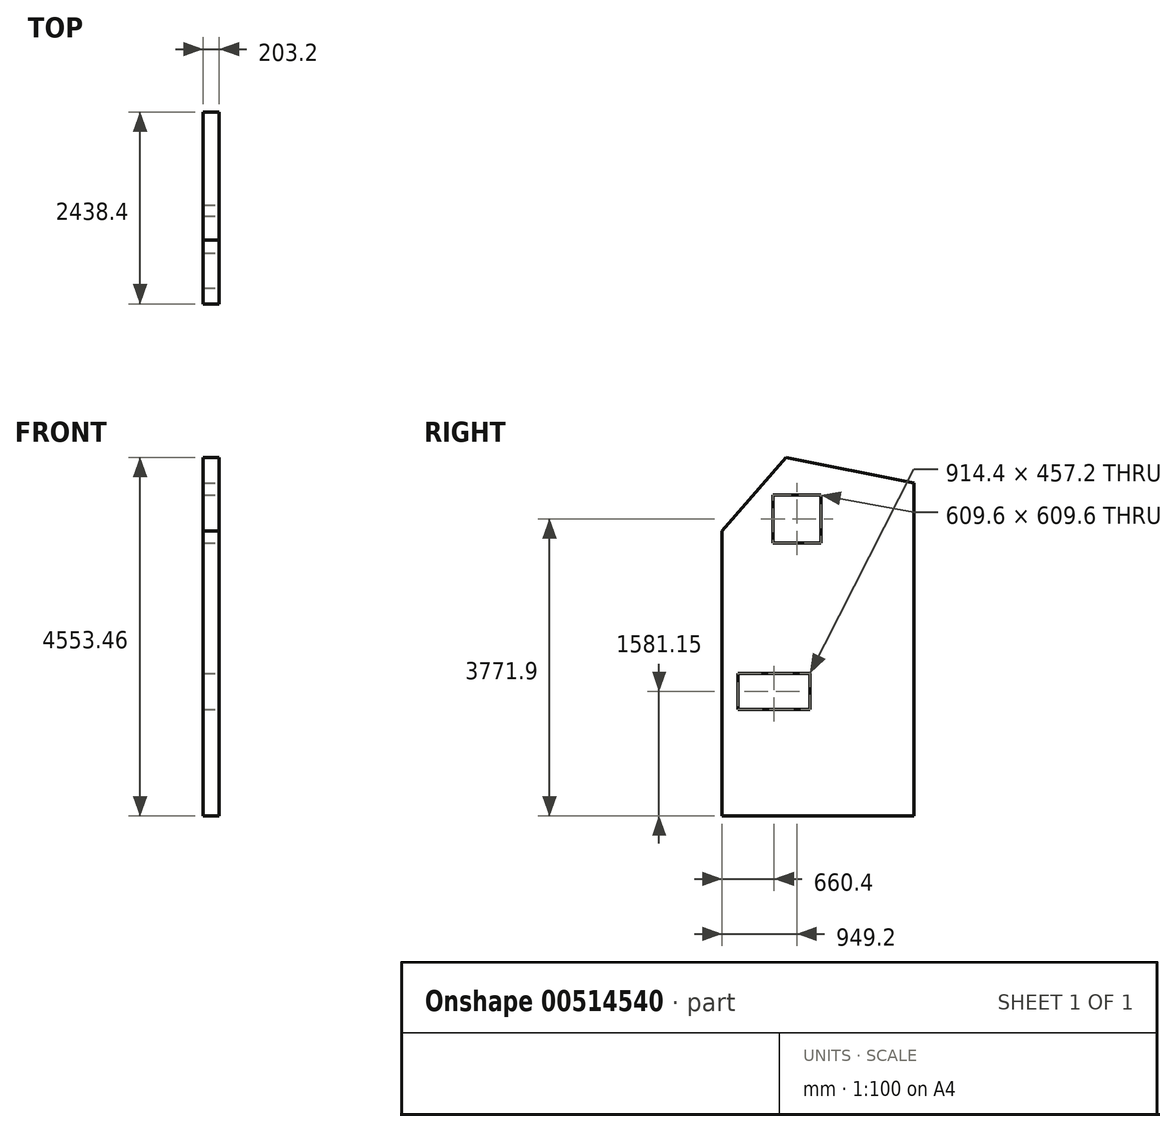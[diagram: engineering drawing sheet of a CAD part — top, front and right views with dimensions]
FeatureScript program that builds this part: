
annotation { "Feature Type Name" : "Feature", "Feature Type Description" : "" }
export const myFeature = defineFeature(function(context is Context, id is Id, definition is map)
    precondition{}
    {
        {
            var Q0;
            Q0=qCreatedBy(makeId("Right.planeOp"),FACE);
            var sketch = newSketch(context, id + "F0", { "sketchPlane" : qUnion([Q0])});
            skLineSegment(sketch, "E0.bottom", {"start": v(1219.2, 2353.82) * mm, "end": v(-1219.2, 2353.82) * mm});
            skLineSegment(sketch, "E0.top", {"start": v(1219.2, -2353.82) * mm, "end": v(-1219.2, -2353.82) * mm});
            skLineSegment(sketch, "E0.left", {"start": v(1219.2, 2353.82) * mm, "end": v(1219.2, -2353.82) * mm});
            skLineSegment(sketch, "E0.right", {"start": v(-1219.2, 2353.82) * mm, "end": v(-1219.2, -2353.82) * mm});
            skPoint(sketch, "E0.middle", {"position": v(0, 0) * mm});
            skSolve(sketch);
        }
        {
            var Q0;
            Q0=makeQuery(id+"F0.imprint","IMPRINT",FACE,{"disambiguationData":[TD([[makeQuery(id+"F0.imprint","IMPRINT",EDGE,{"derivedFrom":sQuery(id+"F0.wireOp",EDGE,"E0.bottom")}),1.0]])]});
            extrude(context, id + "F1", {"entities" : qUnion([Q0]), "depth" : 203.2 * mm, "offsetDistance" : 25.4 * mm});
        }
        {
            var Q0;
            Q0=qCreatedBy(makeId("Front.planeOp"),FACE);
            var sketch = newSketch(context, id + "F2", { "sketchPlane" : qUnion([Q0])});
            skLineSegment(sketch, "E1", {"start": v(0, 0) * mm, "end": v(0, -38) * mm});
            skSolve(sketch);
        }
        {
            var Q0;
            Q0=makeQuery(id+"F1.opExtrude","SWEPT_BODY",BODY,{"disambiguationData":[OSD([sQuery(id+"F0.wireOp",EDGE,"E0.bottom"),sQuery(id+"F0.wireOp",EDGE,"E0.top"),sQuery(id+"F0.wireOp",EDGE,"E0.left"),sQuery(id+"F0.wireOp",EDGE,"E0.right")])]});
            var Q1;
            Q1=sQuery(id+"F2.wireOp",EDGE,"E1");
            transform(context, id + "F3", {"entities" : qUnion([Q0]), "transformType" : TransformType.ROTATION, "transformAxis" : qUnion([Q1]), "angle" : 180 * degree, "makeCopy" : false});
        }
        {
            var Q0;
            Q0=makeQuery(id+"F1.opExtrude","CAP_FACE",FACE,{"disambiguationData":[OSD([sQuery(id+"F0.wireOp",EDGE,"E0.bottom"),sQuery(id+"F0.wireOp",EDGE,"E0.top"),sQuery(id+"F0.wireOp",EDGE,"E0.left"),sQuery(id+"F0.wireOp",EDGE,"E0.right")])],"isStart":true});
            var sketch = newSketch(context, id + "F4", { "sketchPlane" : qUnion([Q0])});
            skLineSegment(sketch, "E2", {"start": v(-407.32, 276.86) * mm, "end": v(-407.32, 46.48) * mm});
            skLineSegment(sketch, "E3", {"start": v(-407.32, 2199.64) * mm, "end": v(-407.32, 46.48) * mm});
            skLineSegment(sketch, "E4", {"start": v(1219.2, 46.48) * mm, "end": v(1219.2, 1875.28) * mm});
            skLineSegment(sketch, "E5", {"start": v(-1219.2, 46.48) * mm, "end": v(-1219.2, 1265.68) * mm});
            skLineSegment(sketch, "E6", {"start": v(-1219.2, 46.48) * mm, "end": v(-407.32, 46.48) * mm});
            skLineSegment(sketch, "E7", {"start": v(-1219.2, 1265.68) * mm, "end": v(-407.32, 2199.64) * mm});
            skLineSegment(sketch, "E8", {"start": v(-1219.2, 1265.68) * mm, "end": v(-407.32, 1265.68) * mm});
            skLineSegment(sketch, "E9", {"start": v(1219.2, 1875.28) * mm, "end": v(-407.32, 2199.64) * mm});
            skSolve(sketch);
        }
        {
            var Q0;
            {var subQ3=sQuery(id+"F4.wireOp",EDGE,"E7");Q0=makeQuery(id+"F4.imprint","IMPRINT",FACE,{"disambiguationData":[TD([[makeQuery(id+"F4.imprint","IMPRINT",EDGE,{"derivedFrom":subQ3}),1.0]])]});}
            extrude(context, id + "F5", {"entities" : qUnion([Q0]), "operationType" : NewBodyOperationType.REMOVE, "oppositeDirection" : true, "depth" : 203.2 * mm, "offsetDistance" : 25.4 * mm});
        }
        {
            var Q0;
            Q0=makeQuery(id+"F1.opExtrude","CAP_FACE",FACE,{"disambiguationData":[OSD([sQuery(id+"F0.wireOp",EDGE,"E0.bottom"),sQuery(id+"F0.wireOp",EDGE,"E0.top"),sQuery(id+"F0.wireOp",EDGE,"E0.left"),sQuery(id+"F0.wireOp",EDGE,"E0.right")])],"isStart":true});
            var sketch = newSketch(context, id + "F6", { "sketchPlane" : qUnion([Q0])});
            skLineSegment(sketch, "E10", {"start": v(-1219.2, -2353.82) * mm, "end": v(-1219.2, -2068.07) * mm});
            skLineSegment(sketch, "E11", {"start": v(-1219.2, -2068.07) * mm, "end": v(-1219.2, -1153.67) * mm});
            skLineSegment(sketch, "E12", {"start": v(-1219.2, -1153.67) * mm, "end": v(-1219.2, -1001.27) * mm});
            skLineSegment(sketch, "E13", {"start": v(-1219.2, -1001.27) * mm, "end": v(-1016, -1001.27) * mm});
            skLineSegment(sketch, "E14.bottom", {"start": v(-1016, -1001.27) * mm, "end": v(-101.6, -1001.27) * mm});
            skLineSegment(sketch, "E14.top", {"start": v(-1016, -544.07) * mm, "end": v(-101.6, -544.07) * mm});
            skLineSegment(sketch, "E14.left", {"start": v(-1016, -1001.27) * mm, "end": v(-1016, -544.07) * mm});
            skLineSegment(sketch, "E14.right", {"start": v(-101.6, -1001.27) * mm, "end": v(-101.6, -544.07) * mm});
            skSolve(sketch);
        }
        {
            var Q0;
            Q0=makeQuery(id+"F6.imprint","IMPRINT",FACE,{"disambiguationData":[TD([[makeQuery(id+"F6.imprint","IMPRINT",EDGE,{"derivedFrom":sQuery(id+"F6.wireOp",EDGE,"E14.bottom")}),1.0]])]});
            extrude(context, id + "F7", {"entities" : qUnion([Q0]), "operationType" : NewBodyOperationType.REMOVE, "oppositeDirection" : true, "depth" : 203.2 * mm, "offsetDistance" : 25.4 * mm});
        }
        {
            var Q0;
            Q0=makeQuery(id+"F1.opExtrude","CAP_FACE",FACE,{"disambiguationData":[OSD([sQuery(id+"F0.wireOp",EDGE,"E0.bottom"),sQuery(id+"F0.wireOp",EDGE,"E0.top"),sQuery(id+"F0.wireOp",EDGE,"E0.left"),sQuery(id+"F0.wireOp",EDGE,"E0.right")])],"isStart":true});
            var sketch = newSketch(context, id + "F8", { "sketchPlane" : qUnion([Q0])});
            skLineSegment(sketch, "E15", {"start": v(-1219.2, 1265.68) * mm, "end": v(-1016, 1265.68) * mm});
            skLineSegment(sketch, "E16", {"start": v(-1016, 1265.68) * mm, "end": v(-711.2, 1265.68) * mm});
            skLineSegment(sketch, "E17", {"start": v(-270, -2353.82) * mm, "end": v(-270, -2068.07) * mm});
            skLineSegment(sketch, "E18", {"start": v(-270, -2068.07) * mm, "end": v(-270, -239.27) * mm});
            skLineSegment(sketch, "E19", {"start": v(-270, -239.27) * mm, "end": v(-270, 46.48) * mm});
            skLineSegment(sketch, "E20", {"start": v(-270, 46.48) * mm, "end": v(-270, 1113.28) * mm});
            skLineSegment(sketch, "E21.bottom", {"start": v(-270, 1113.28) * mm, "end": v(-574.8, 1113.28) * mm});
            skLineSegment(sketch, "E21.top", {"start": v(-270, 1722.88) * mm, "end": v(-574.8, 1722.88) * mm});
            skLineSegment(sketch, "E21.left", {"start": v(-270, 1113.28) * mm, "end": v(-270, 1722.88) * mm});
            skLineSegment(sketch, "E21.right", {"start": v(-574.8, 1113.28) * mm, "end": v(-574.8, 1722.88) * mm});
            skLineSegment(sketch, "E22.bottom", {"start": v(-270, 1722.88) * mm, "end": v(34.8, 1722.88) * mm});
            skLineSegment(sketch, "E22.top", {"start": v(-270, 1113.28) * mm, "end": v(34.8, 1113.28) * mm});
            skLineSegment(sketch, "E22.left", {"start": v(-270, 1722.88) * mm, "end": v(-270, 1113.28) * mm});
            skLineSegment(sketch, "E22.right", {"start": v(34.8, 1722.88) * mm, "end": v(34.8, 1113.28) * mm});
            skSolve(sketch);
        }
        {
            var Q0;
            Q0=makeQuery(id+"F8.imprint","IMPRINT",FACE,{"disambiguationData":[TD([[makeQuery(id+"F8.imprint","IMPRINT",EDGE,{"derivedFrom":sQuery(id+"F8.wireOp",EDGE,"E21.bottom")}),-1.0]])]});
            var Q1;
            Q1=makeQuery(id+"F8.imprint","IMPRINT",FACE,{"disambiguationData":[TD([[makeQuery(id+"F8.imprint","IMPRINT",EDGE,{"derivedFrom":sQuery(id+"F8.wireOp",EDGE,"E22.bottom")}),-1.0]])]});
            extrude(context, id + "F9", {"entities" : qUnion([Q0, Q1]), "operationType" : NewBodyOperationType.REMOVE, "oppositeDirection" : true, "depth" : 203.2 * mm, "offsetDistance" : 25.4 * mm});
        }
    });
